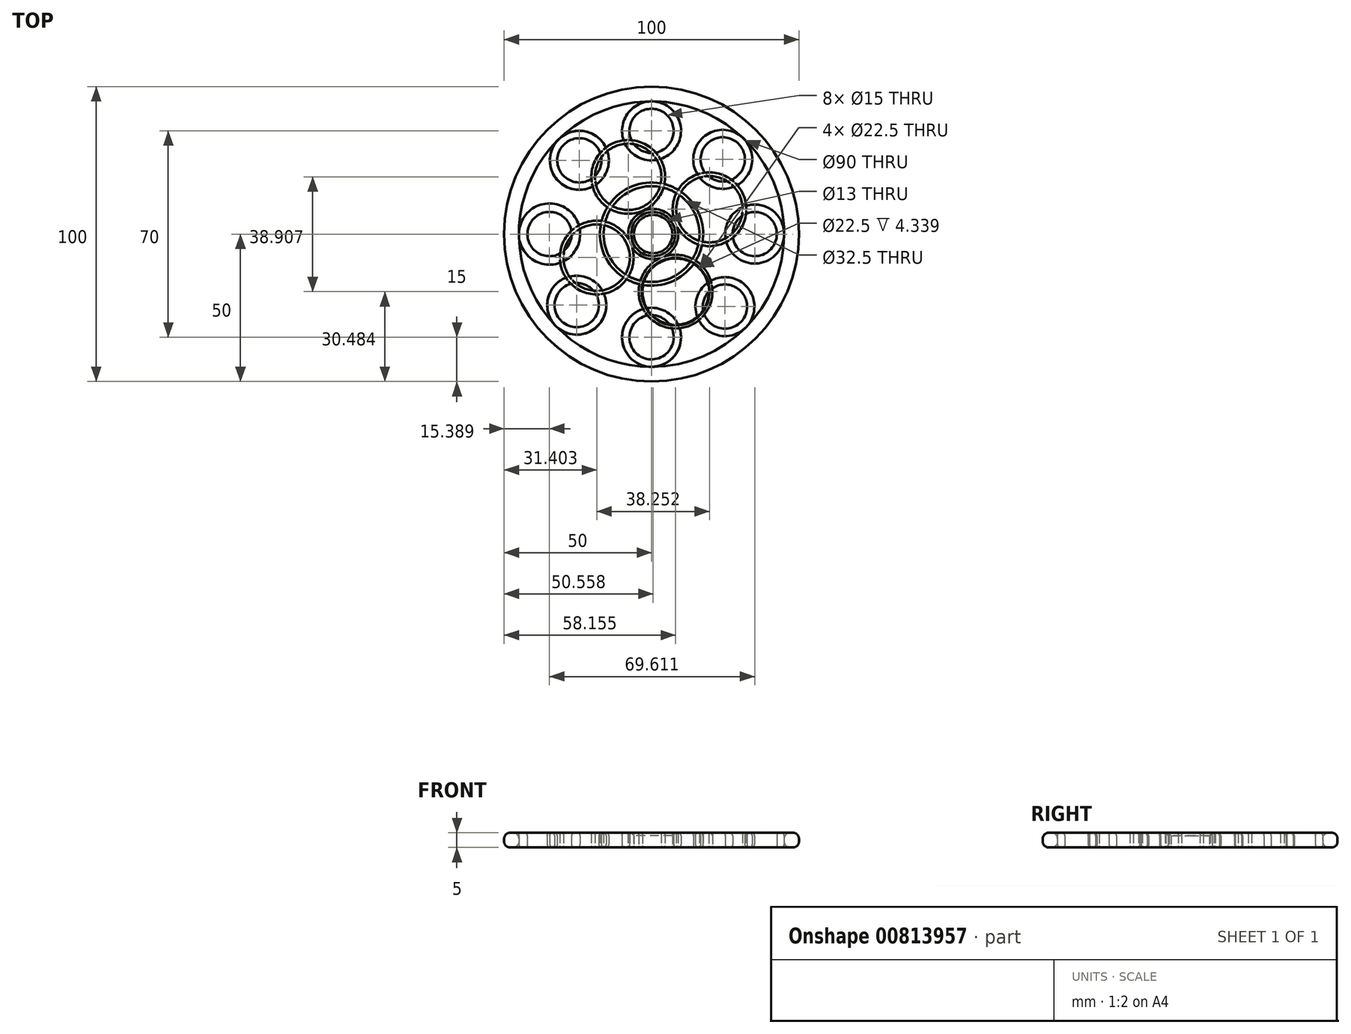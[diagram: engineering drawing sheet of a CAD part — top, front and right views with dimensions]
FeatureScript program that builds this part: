
annotation { "Feature Type Name" : "Feature", "Feature Type Description" : "" }
export const myFeature = defineFeature(function(context is Context, id is Id, definition is map)
    precondition{}
    {
        {
            var Q0;
            Q0=qCreatedBy(makeId("Top.planeOp"),FACE);
            var sketch = newSketch(context, id + "F0", { "sketchPlane" : qUnion([Q0])});
            skCircle(sketch, "E0", {"center": v(0, 0) * mm, "radius": 50 * mm});
            skCircle(sketch, "E1", {"center": v(0, 0) * mm, "radius": 45 * mm});
            skSolve(sketch);
        }
        {
            var Q0;
            Q0=makeQuery(id+"F0.imprint","IMPRINT",FACE,{"disambiguationData":[TD([[makeQuery(id+"F0.imprint","IMPRINT",EDGE,{"derivedFrom":sQuery(id+"F0.wireOp",EDGE,"E0")}),1.0]])]});
            extrude(context, id + "F1", {"entities" : qUnion([Q0]), "depth" : 5 * mm, "offsetDistance" : 25 * mm});
        }
        {
            var Q0;
            Q0=qCreatedBy(makeId("Top.planeOp"),FACE);
            var sketch = newSketch(context, id + "F2", { "sketchPlane" : qUnion([Q0])});
            skCircle(sketch, "E2", {"center": v(35, 0) * mm, "radius": 10 * mm});
            skCircle(sketch, "E3", {"center": v(35, 0) * mm, "radius": 7.5 * mm});
            skSolve(sketch);
        }
        {
            var Q0;
            Q0=makeQuery(id+"F2.imprint","IMPRINT",FACE,{"disambiguationData":[TD([[makeQuery(id+"F2.imprint","IMPRINT",EDGE,{"derivedFrom":sQuery(id+"F2.wireOp",EDGE,"E2")}),1.0]])]});
            extrude(context, id + "F3", {"entities" : qUnion([Q0]), "operationType" : NewBodyOperationType.ADD, "depth" : 5 * mm, "offsetDistance" : 25 * mm});
        }
        {
            var Q0;
            Q0=qCreatedBy(makeId("Top.planeOp"),FACE);
            var sketch = newSketch(context, id + "F4", { "sketchPlane" : qUnion([Q0])});
            skCircle(sketch, "E4", {"center": v(0, 35) * mm, "radius": 10 * mm});
            skCircle(sketch, "E5", {"center": v(0, 35) * mm, "radius": 7.5 * mm});
            skSolve(sketch);
        }
        {
            var Q0;
            Q0=makeQuery(id+"F4.imprint","IMPRINT",FACE,{"disambiguationData":[TD([[makeQuery(id+"F4.imprint","IMPRINT",EDGE,{"derivedFrom":sQuery(id+"F4.wireOp",EDGE,"E4")}),1.0]])]});
            extrude(context, id + "F5", {"entities" : qUnion([Q0]), "operationType" : NewBodyOperationType.ADD, "depth" : 5 * mm, "offsetDistance" : 25 * mm});
        }
        {
            var Q0;
            Q0=qCreatedBy(makeId("Top.planeOp"),FACE);
            var sketch = newSketch(context, id + "F6", { "sketchPlane" : qUnion([Q0])});
            skCircle(sketch, "E6", {"center": v(-34.61, 0) * mm, "radius": 10.39 * mm});
            skCircle(sketch, "E7", {"center": v(-34.61, 0) * mm, "radius": 7.5 * mm});
            skSolve(sketch);
        }
        {
            var Q0;
            Q0=sQuery(id+"F6.wireOp",EDGE,"E6");
            var Q1;
            Q1=sQuery(id+"F6.wireOp",EDGE,"E7");
            extrude(context, id + "F7", {"bodyType" : ToolBodyType.SURFACE, "surfaceEntities" : qUnion([Q0, Q1]), "depth" : 5 * mm, "offsetDistance" : 25 * mm});
        }
        {
            var Q0;
            Q0=makeQuery(id+"F6.imprint","IMPRINT",FACE,{"disambiguationData":[TD([[makeQuery(id+"F6.imprint","IMPRINT",EDGE,{"derivedFrom":sQuery(id+"F6.wireOp",EDGE,"E6")}),1.0]])]});
            extrude(context, id + "F8", {"entities" : qUnion([Q0]), "operationType" : NewBodyOperationType.ADD, "depth" : 5 * mm, "offsetDistance" : 25 * mm});
        }
        {
            var Q0;
            Q0=qCreatedBy(makeId("Top.planeOp"),FACE);
            var sketch = newSketch(context, id + "F9", { "sketchPlane" : qUnion([Q0])});
            skCircle(sketch, "E8", {"center": v(0, -35) * mm, "radius": 10 * mm});
            skCircle(sketch, "E9", {"center": v(0, -35) * mm, "radius": 7.5 * mm});
            skSolve(sketch);
        }
        {
            var Q0;
            Q0=makeQuery(id+"F9.imprint","IMPRINT",FACE,{"disambiguationData":[TD([[makeQuery(id+"F9.imprint","IMPRINT",EDGE,{"derivedFrom":sQuery(id+"F9.wireOp",EDGE,"E8")}),1.0]])]});
            extrude(context, id + "F10", {"entities" : qUnion([Q0]), "operationType" : NewBodyOperationType.ADD, "depth" : 5 * mm, "offsetDistance" : 25 * mm});
        }
        {
            var Q0;
            Q0=qCreatedBy(makeId("Top.planeOp"),FACE);
            var sketch = newSketch(context, id + "F11", { "sketchPlane" : qUnion([Q0])});
            skCircle(sketch, "E10", {"center": v(-25.37, -24.1) * mm, "radius": 10 * mm});
            skCircle(sketch, "E11", {"center": v(-25.37, -24.1) * mm, "radius": 7.5 * mm});
            skSolve(sketch);
        }
        {
            var Q0;
            Q0=makeQuery(id+"F11.imprint","IMPRINT",FACE,{"disambiguationData":[TD([[makeQuery(id+"F11.imprint","IMPRINT",EDGE,{"derivedFrom":sQuery(id+"F11.wireOp",EDGE,"E10")}),1.0]])]});
            extrude(context, id + "F12", {"entities" : qUnion([Q0]), "operationType" : NewBodyOperationType.ADD, "depth" : 5 * mm, "offsetDistance" : 25 * mm});
        }
        {
            var Q0;
            Q0=qCreatedBy(makeId("Top.planeOp"),FACE);
            var sketch = newSketch(context, id + "F13", { "sketchPlane" : qUnion([Q0])});
            skCircle(sketch, "E12", {"center": v(-24.49, 25) * mm, "radius": 10 * mm});
            skCircle(sketch, "E13", {"center": v(-24.49, 25) * mm, "radius": 7.5 * mm});
            skSolve(sketch);
        }
        {
            var Q0;
            Q0=makeQuery(id+"F13.imprint","IMPRINT",FACE,{"disambiguationData":[TD([[makeQuery(id+"F13.imprint","IMPRINT",EDGE,{"derivedFrom":sQuery(id+"F13.wireOp",EDGE,"E12")}),1.0]])]});
            extrude(context, id + "F14", {"entities" : qUnion([Q0]), "operationType" : NewBodyOperationType.ADD, "depth" : 5 * mm, "offsetDistance" : 25 * mm});
        }
        {
            var Q0;
            Q0=qCreatedBy(makeId("Top.planeOp"),FACE);
            var sketch = newSketch(context, id + "F15", { "sketchPlane" : qUnion([Q0])});
            skCircle(sketch, "E14", {"center": v(24.9, -24.6) * mm, "radius": 10 * mm});
            skCircle(sketch, "E15", {"center": v(24.9, -24.6) * mm, "radius": 7.5 * mm});
            skSolve(sketch);
        }
        {
            var Q0;
            Q0=makeQuery(id+"F15.imprint","IMPRINT",FACE,{"disambiguationData":[TD([[makeQuery(id+"F15.imprint","IMPRINT",EDGE,{"derivedFrom":sQuery(id+"F15.wireOp",EDGE,"E14")}),1.0]])]});
            extrude(context, id + "F16", {"entities" : qUnion([Q0]), "operationType" : NewBodyOperationType.ADD, "depth" : 5 * mm, "offsetDistance" : 25 * mm});
        }
        {
            var Q0;
            Q0=qCreatedBy(makeId("Top.planeOp"),FACE);
            var sketch = newSketch(context, id + "F17", { "sketchPlane" : qUnion([Q0])});
            skCircle(sketch, "E16", {"center": v(24.16, 25.32) * mm, "radius": 10 * mm});
            skCircle(sketch, "E17", {"center": v(24.16, 25.32) * mm, "radius": 7.5 * mm});
            skSolve(sketch);
        }
        {
            var Q0;
            Q0=makeQuery(id+"F17.imprint","IMPRINT",FACE,{"disambiguationData":[TD([[makeQuery(id+"F17.imprint","IMPRINT",EDGE,{"derivedFrom":sQuery(id+"F17.wireOp",EDGE,"E16")}),1.0]])]});
            extrude(context, id + "F18", {"entities" : qUnion([Q0]), "operationType" : NewBodyOperationType.ADD, "depth" : 5 * mm, "offsetDistance" : 25 * mm});
        }
        {
            var Q0;
            Q0=qCreatedBy(makeId("Top.planeOp"),FACE);
            var sketch = newSketch(context, id + "F19", { "sketchPlane" : qUnion([Q0])});
            skCircle(sketch, "E18", {"center": v(-18.6, -7.97) * mm, "radius": 12.5 * mm});
            skCircle(sketch, "E19", {"center": v(-18.6, -7.97) * mm, "radius": 11.25 * mm});
            skCircle(sketch, "E20", {"center": v(-18.6, -7.97) * mm, "radius": 7.5 * mm});
            skSolve(sketch);
        }
        {
            var Q0;
            Q0=makeQuery(id+"F19.imprint","IMPRINT",FACE,{"disambiguationData":[TD([[makeQuery(id+"F19.imprint","IMPRINT",EDGE,{"derivedFrom":sQuery(id+"F19.wireOp",EDGE,"E18")}),1.0]])]});
            extrude(context, id + "F20", {"entities" : qUnion([Q0]), "depth" : 5 * mm, "offsetDistance" : 25 * mm});
        }
        {
            var Q0;
            Q0=qCreatedBy(makeId("Top.planeOp"),FACE);
            var sketch = newSketch(context, id + "F21", { "sketchPlane" : qUnion([Q0])});
            skCircle(sketch, "E21", {"center": v(8.16, -19.52) * mm, "radius": 12.5 * mm});
            skCircle(sketch, "E22", {"center": v(8.16, -19.52) * mm, "radius": 11.25 * mm});
            skCircle(sketch, "E23", {"center": v(8.16, -19.52) * mm, "radius": 7.5 * mm});
            skSolve(sketch);
        }
        {
            var Q0;
            Q0=makeQuery(id+"F21.imprint","IMPRINT",FACE,{"disambiguationData":[TD([[makeQuery(id+"F21.imprint","IMPRINT",EDGE,{"derivedFrom":sQuery(id+"F21.wireOp",EDGE,"E21")}),1.0]])]});
            extrude(context, id + "F22", {"entities" : qUnion([Q0]), "depth" : 5 * mm, "offsetDistance" : 25 * mm});
        }
        {
            var Q0;
            Q0=qCreatedBy(makeId("Top.planeOp"),FACE);
            var sketch = newSketch(context, id + "F23", { "sketchPlane" : qUnion([Q0])});
            skCircle(sketch, "E24", {"center": v(19.65, 8.41) * mm, "radius": 12.5 * mm});
            skCircle(sketch, "E25", {"center": v(19.65, 8.41) * mm, "radius": 11.25 * mm});
            skCircle(sketch, "E26", {"center": v(19.65, 8.41) * mm, "radius": 7.5 * mm});
            skSolve(sketch);
        }
        {
            var Q0;
            Q0=makeQuery(id+"F23.imprint","IMPRINT",FACE,{"disambiguationData":[TD([[makeQuery(id+"F23.imprint","IMPRINT",EDGE,{"derivedFrom":sQuery(id+"F23.wireOp",EDGE,"E24")}),1.0]])]});
            var Q1;
            Q1 = qSketchRegion(id + "F21", true);
            extrude(context, id + "F24", {"entities" : qUnion([Q0, Q1]), "depth" : 5 * mm, "offsetDistance" : 25 * mm});
        }
        {
            var Q0;
            Q0=qCreatedBy(makeId("Top.planeOp"),FACE);
            var sketch = newSketch(context, id + "F25", { "sketchPlane" : qUnion([Q0])});
            skCircle(sketch, "E27", {"center": v(-7.91, 19.4) * mm, "radius": 12.5 * mm});
            skCircle(sketch, "E28", {"center": v(-7.91, 19.4) * mm, "radius": 11.25 * mm});
            skCircle(sketch, "E29", {"center": v(-7.91, 19.4) * mm, "radius": 7.5 * mm});
            skSolve(sketch);
        }
        {
            var Q0;
            Q0=makeQuery(id+"F25.imprint","IMPRINT",FACE,{"disambiguationData":[TD([[makeQuery(id+"F25.imprint","IMPRINT",EDGE,{"derivedFrom":sQuery(id+"F25.wireOp",EDGE,"E27")}),1.0]])]});
            extrude(context, id + "F26", {"entities" : qUnion([Q0]), "depth" : 5 * mm, "offsetDistance" : 25 * mm});
        }
        {
            var Q0;
            Q0=qCreatedBy(makeId("Top.planeOp"),FACE);
            var sketch = newSketch(context, id + "F27", { "sketchPlane" : qUnion([Q0])});
            skCircle(sketch, "E30", {"center": v(0, 0) * mm, "radius": 17.5 * mm});
            skCircle(sketch, "E31", {"center": v(0, 0) * mm, "radius": 16.25 * mm});
            skCircle(sketch, "E32", {"center": v(0, 0) * mm, "radius": 8.5 * mm});
            skCircle(sketch, "E33", {"center": v(0, 0) * mm, "radius": 4.68 * mm});
            skSolve(sketch);
        }
        {
            var Q0;
            Q0=makeQuery(id+"F27.imprint","IMPRINT",FACE,{"disambiguationData":[TD([[makeQuery(id+"F27.imprint","IMPRINT",EDGE,{"derivedFrom":sQuery(id+"F27.wireOp",EDGE,"E30")}),1.0]])]});
            extrude(context, id + "F28", {"entities" : qUnion([Q0]), "depth" : 5 * mm, "offsetDistance" : 25 * mm});
        }
        {
            var Q0;
            Q0=qCreatedBy(makeId("Top.planeOp"),FACE);
            var sketch = newSketch(context, id + "F29", { "sketchPlane" : qUnion([Q0])});
            skCircle(sketch, "E34", {"center": v(0.56, 0) * mm, "radius": 8.5 * mm});
            skCircle(sketch, "E35", {"center": v(0.56, 0) * mm, "radius": 6.5 * mm});
            skSolve(sketch);
        }
        {
            var Q0;
            Q0=makeQuery(id+"F29.imprint","IMPRINT",FACE,{"disambiguationData":[TD([[makeQuery(id+"F29.imprint","IMPRINT",EDGE,{"derivedFrom":sQuery(id+"F29.wireOp",EDGE,"E34")}),1.0]])]});
            extrude(context, id + "F30", {"entities" : qUnion([Q0]), "depth" : 5 * mm, "offsetDistance" : 25 * mm});
        }
        {
            var Q0;
            Q0=makeQuery(id+"F30.opExtrude","CAP_EDGE",EDGE,{"disambiguationData":[OSD([sQuery(id+"F29.wireOp",EDGE,"E35")])],"isStart":false});
            chamfer(context, id + "F31", {"entities" : qUnion([Q0]), "width" : 1 * mm, "tangentPropagation" : true});
        }
        {
            var Q0;
            Q0=makeQuery(id+"F12.opExtrude","CAP_EDGE",EDGE,{"disambiguationData":[OSD([sQuery(id+"F11.wireOp",EDGE,"E10")])],"isStart":false});
            var Q1;
            Q1=makeQuery(id+"F12.opExtrude","CAP_EDGE",EDGE,{"disambiguationData":[OSD([sQuery(id+"F11.wireOp",EDGE,"E11")])],"isStart":false});
            var Q2;
            Q2=makeQuery(id+"F10.opExtrude","CAP_EDGE",EDGE,{"disambiguationData":[OSD([sQuery(id+"F9.wireOp",EDGE,"E9")])],"isStart":false});
            var Q3;
            Q3=makeQuery(id+"F10.opExtrude","CAP_EDGE",EDGE,{"disambiguationData":[OSD([sQuery(id+"F9.wireOp",EDGE,"E8")])],"isStart":false});
            var Q4;
            Q4=makeQuery(id+"F16.opExtrude","CAP_EDGE",EDGE,{"disambiguationData":[OSD([sQuery(id+"F15.wireOp",EDGE,"E14")])],"isStart":false});
            var Q5;
            Q5=makeQuery(id+"F16.opExtrude","CAP_EDGE",EDGE,{"disambiguationData":[OSD([sQuery(id+"F15.wireOp",EDGE,"E15")])],"isStart":false});
            var Q6;
            Q6=makeQuery(id+"F3.opExtrude","CAP_EDGE",EDGE,{"disambiguationData":[OSD([sQuery(id+"F2.wireOp",EDGE,"E2")])],"isStart":false});
            var Q7;
            Q7=makeQuery(id+"F3.opExtrude","CAP_EDGE",EDGE,{"disambiguationData":[OSD([sQuery(id+"F2.wireOp",EDGE,"E3")])],"isStart":false});
            var Q8;
            Q8=makeQuery(id+"F18.opExtrude","CAP_EDGE",EDGE,{"disambiguationData":[OSD([sQuery(id+"F17.wireOp",EDGE,"E16")])],"isStart":false});
            var Q9;
            Q9=makeQuery(id+"F18.opExtrude","CAP_EDGE",EDGE,{"disambiguationData":[OSD([sQuery(id+"F17.wireOp",EDGE,"E17")])],"isStart":false});
            var Q10;
            Q10=makeQuery(id+"F5.opExtrude","CAP_EDGE",EDGE,{"disambiguationData":[OSD([sQuery(id+"F4.wireOp",EDGE,"E4")])],"isStart":false});
            var Q11;
            Q11=makeQuery(id+"F5.opExtrude","CAP_EDGE",EDGE,{"disambiguationData":[OSD([sQuery(id+"F4.wireOp",EDGE,"E5")])],"isStart":false});
            var Q12;
            Q12=makeQuery(id+"F14.opExtrude","CAP_EDGE",EDGE,{"disambiguationData":[OSD([sQuery(id+"F13.wireOp",EDGE,"E12")])],"isStart":false});
            var Q13;
            Q13=makeQuery(id+"F14.opExtrude","CAP_EDGE",EDGE,{"disambiguationData":[OSD([sQuery(id+"F13.wireOp",EDGE,"E13")])],"isStart":false});
            fillet(context, id + "F32", {"entities" : qUnion([Q0, Q1, Q2, Q3, Q4, Q5, Q6, Q7, Q8, Q9, Q10, Q11, Q12, Q13]), "radius" : 1 * mm, "tangentPropagation" : true, "allowEdgeOverflow" : false});
        }
        {
            var Q0;
            Q0=makeQuery(id+"F8.opExtrude","CAP_FACE",FACE,{"disambiguationData":[OSD([sQuery(id+"F6.wireOp",EDGE,"E6"),sQuery(id+"F6.wireOp",EDGE,"E7")])],"isStart":false});
            fillet(context, id + "F33", {"entities" : qUnion([Q0]), "radius" : 1 * mm, "tangentPropagation" : true, "allowEdgeOverflow" : false});
        }
        {
            var Q0;
            Q0=makeQuery(id+"F1.opExtrude","CAP_EDGE",EDGE,{"disambiguationData":[OSD([sQuery(id+"F0.wireOp",EDGE,"E1")])],"isStart":false});
            var Q1;
            Q1=makeQuery(id+"F1.opExtrude","CAP_EDGE",EDGE,{"disambiguationData":[OSD([sQuery(id+"F0.wireOp",EDGE,"E0")])],"isStart":false});
            fillet(context, id + "F34", {"entities" : qUnion([Q0, Q1]), "radius" : 2 * mm, "tangentPropagation" : true, "allowEdgeOverflow" : false});
        }
        {
            var Q0;
            Q0=makeQuery(id+"F22.opExtrude","CAP_EDGE",EDGE,{"disambiguationData":[OSD([sQuery(id+"F21.wireOp",EDGE,"E21")])],"isStart":false});
            var Q1;
            Q1=makeQuery(id+"F22.opExtrude","CAP_EDGE",EDGE,{"disambiguationData":[OSD([sQuery(id+"F21.wireOp",EDGE,"E22")])],"isStart":false});
            var Q2;
            Q2=makeQuery(id+"F28.opExtrude","CAP_EDGE",EDGE,{"disambiguationData":[OSD([sQuery(id+"F27.wireOp",EDGE,"E30")])],"isStart":false});
            var Q3;
            Q3=makeQuery(id+"F28.opExtrude","CAP_EDGE",EDGE,{"disambiguationData":[OSD([sQuery(id+"F27.wireOp",EDGE,"E31")])],"isStart":false});
            var Q4;
            Q4=makeQuery(id+"F20.opExtrude","CAP_EDGE",EDGE,{"disambiguationData":[OSD([sQuery(id+"F19.wireOp",EDGE,"E18")])],"isStart":false});
            var Q5;
            Q5=makeQuery(id+"F20.opExtrude","CAP_EDGE",EDGE,{"disambiguationData":[OSD([sQuery(id+"F19.wireOp",EDGE,"E19")])],"isStart":false});
            var Q6;
            Q6=makeQuery(id+"F24.opExtrude","CAP_EDGE",EDGE,{"disambiguationData":[OSD([sQuery(id+"F23.wireOp",EDGE,"E24")])],"isStart":false});
            var Q7;
            Q7=makeQuery(id+"F24.opExtrude","CAP_EDGE",EDGE,{"disambiguationData":[OSD([sQuery(id+"F23.wireOp",EDGE,"E25")])],"isStart":false});
            var Q8;
            Q8=makeQuery(id+"F26.opExtrude","CAP_EDGE",EDGE,{"disambiguationData":[OSD([sQuery(id+"F25.wireOp",EDGE,"E28")])],"isStart":false});
            var Q9;
            Q9=makeQuery(id+"F26.opExtrude","CAP_EDGE",EDGE,{"disambiguationData":[OSD([sQuery(id+"F25.wireOp",EDGE,"E27")])],"isStart":false});
            var Q10;
            Q10=makeQuery(id+"F30.opExtrude","CAP_EDGE",EDGE,{"disambiguationData":[OSD([sQuery(id+"F29.wireOp",EDGE,"E34")])],"isStart":false});
            fillet(context, id + "F35", {"entities" : qUnion([Q0, Q1, Q2, Q3, Q4, Q5, Q6, Q7, Q8, Q9, Q10]), "radius" : .5 * mm, "tangentPropagation" : true, "allowEdgeOverflow" : false});
        }
        {
            var Q0;
            Q0=makeQuery(id+"F1.opExtrude","CAP_EDGE",EDGE,{"disambiguationData":[OSD([sQuery(id+"F0.wireOp",EDGE,"E0")])],"isStart":true});
            var Q1;
            Q1=makeQuery(id+"F1.opExtrude","CAP_EDGE",EDGE,{"disambiguationData":[OSD([sQuery(id+"F0.wireOp",EDGE,"E1")])],"isStart":true});
            fillet(context, id + "F36", {"entities" : qUnion([Q0, Q1]), "radius" : 2 * mm, "tangentPropagation" : true, "allowEdgeOverflow" : false});
        }
        {
            var Q0;
            Q0=makeQuery(id+"F14.opExtrude","CAP_EDGE",EDGE,{"disambiguationData":[OSD([sQuery(id+"F13.wireOp",EDGE,"E12")])],"isStart":true});
            var Q1;
            Q1=makeQuery(id+"F14.opExtrude","CAP_EDGE",EDGE,{"disambiguationData":[OSD([sQuery(id+"F13.wireOp",EDGE,"E13")])],"isStart":true});
            var Q2;
            Q2=makeQuery(id+"F5.opExtrude","CAP_EDGE",EDGE,{"disambiguationData":[OSD([sQuery(id+"F4.wireOp",EDGE,"E5")])],"isStart":true});
            var Q3;
            Q3=makeQuery(id+"F5.opExtrude","CAP_EDGE",EDGE,{"disambiguationData":[OSD([sQuery(id+"F4.wireOp",EDGE,"E4")])],"isStart":true});
            var Q4;
            Q4=makeQuery(id+"F18.opExtrude","CAP_EDGE",EDGE,{"disambiguationData":[OSD([sQuery(id+"F17.wireOp",EDGE,"E17")])],"isStart":true});
            var Q5;
            Q5=makeQuery(id+"F18.opExtrude","CAP_EDGE",EDGE,{"disambiguationData":[OSD([sQuery(id+"F17.wireOp",EDGE,"E16")])],"isStart":true});
            var Q6;
            Q6=makeQuery(id+"F3.opExtrude","CAP_EDGE",EDGE,{"disambiguationData":[OSD([sQuery(id+"F2.wireOp",EDGE,"E2")])],"isStart":true});
            var Q7;
            Q7=makeQuery(id+"F3.opExtrude","CAP_EDGE",EDGE,{"disambiguationData":[OSD([sQuery(id+"F2.wireOp",EDGE,"E3")])],"isStart":true});
            var Q8;
            Q8=makeQuery(id+"F16.opExtrude","CAP_EDGE",EDGE,{"disambiguationData":[OSD([sQuery(id+"F15.wireOp",EDGE,"E14")])],"isStart":true});
            var Q9;
            Q9=makeQuery(id+"F16.opExtrude","CAP_EDGE",EDGE,{"disambiguationData":[OSD([sQuery(id+"F15.wireOp",EDGE,"E15")])],"isStart":true});
            var Q10;
            Q10=makeQuery(id+"F10.opExtrude","CAP_EDGE",EDGE,{"disambiguationData":[OSD([sQuery(id+"F9.wireOp",EDGE,"E8")])],"isStart":true});
            var Q11;
            Q11=makeQuery(id+"F10.opExtrude","CAP_EDGE",EDGE,{"disambiguationData":[OSD([sQuery(id+"F9.wireOp",EDGE,"E9")])],"isStart":true});
            var Q12;
            Q12=makeQuery(id+"F12.opExtrude","CAP_EDGE",EDGE,{"disambiguationData":[OSD([sQuery(id+"F11.wireOp",EDGE,"E10")])],"isStart":true});
            var Q13;
            Q13=makeQuery(id+"F12.opExtrude","CAP_EDGE",EDGE,{"disambiguationData":[OSD([sQuery(id+"F11.wireOp",EDGE,"E11")])],"isStart":true});
            var Q14;
            Q14=makeQuery(id+"F8.opExtrude","CAP_FACE",FACE,{"disambiguationData":[OSD([sQuery(id+"F6.wireOp",EDGE,"E6"),sQuery(id+"F6.wireOp",EDGE,"E7")])],"isStart":true});
            fillet(context, id + "F37", {"entities" : qUnion([Q0, Q1, Q2, Q3, Q4, Q5, Q6, Q7, Q8, Q9, Q10, Q11, Q12, Q13, Q14]), "radius" : 1 * mm, "tangentPropagation" : true, "allowEdgeOverflow" : false});
        }
        {
            var Q0;
            Q0=makeQuery(id+"F26.opExtrude","CAP_EDGE",EDGE,{"disambiguationData":[OSD([sQuery(id+"F25.wireOp",EDGE,"E27")])],"isStart":true});
            var Q1;
            Q1=makeQuery(id+"F26.opExtrude","CAP_EDGE",EDGE,{"disambiguationData":[OSD([sQuery(id+"F25.wireOp",EDGE,"E28")])],"isStart":true});
            var Q2;
            Q2=makeQuery(id+"F24.opExtrude","CAP_EDGE",EDGE,{"disambiguationData":[OSD([sQuery(id+"F23.wireOp",EDGE,"E25")])],"isStart":true});
            var Q3;
            Q3=makeQuery(id+"F24.opExtrude","CAP_EDGE",EDGE,{"disambiguationData":[OSD([sQuery(id+"F23.wireOp",EDGE,"E24")])],"isStart":true});
            var Q4;
            Q4=makeQuery(id+"F22.opExtrude","CAP_EDGE",EDGE,{"disambiguationData":[OSD([sQuery(id+"F21.wireOp",EDGE,"E22")])],"isStart":true});
            var Q5;
            Q5=makeQuery(id+"F22.opExtrude","CAP_EDGE",EDGE,{"disambiguationData":[OSD([sQuery(id+"F21.wireOp",EDGE,"E21")])],"isStart":true});
            var Q6;
            Q6=makeQuery(id+"F20.opExtrude","CAP_EDGE",EDGE,{"disambiguationData":[OSD([sQuery(id+"F19.wireOp",EDGE,"E18")])],"isStart":true});
            var Q7;
            Q7=makeQuery(id+"F28.opExtrude","CAP_EDGE",EDGE,{"disambiguationData":[OSD([sQuery(id+"F27.wireOp",EDGE,"E30")])],"isStart":true});
            var Q8;
            Q8=makeQuery(id+"F28.opExtrude","CAP_EDGE",EDGE,{"disambiguationData":[OSD([sQuery(id+"F27.wireOp",EDGE,"E31")])],"isStart":true});
            var Q9;
            Q9=makeQuery(id+"F20.opExtrude","CAP_EDGE",EDGE,{"disambiguationData":[OSD([sQuery(id+"F19.wireOp",EDGE,"E19")])],"isStart":true});
            fillet(context, id + "F38", {"entities" : qUnion([Q0, Q1, Q2, Q3, Q4, Q5, Q6, Q7, Q8, Q9]), "radius" : .5 * mm, "tangentPropagation" : true, "allowEdgeOverflow" : false});
        }
        {
            var Q0;
            Q0=makeQuery(id+"F30.opExtrude","CAP_EDGE",EDGE,{"disambiguationData":[OSD([sQuery(id+"F29.wireOp",EDGE,"E34")])],"isStart":true});
            var Q1;
            Q1=makeQuery(id+"F30.opExtrude","CAP_EDGE",EDGE,{"disambiguationData":[OSD([sQuery(id+"F29.wireOp",EDGE,"E35")])],"isStart":true});
            fillet(context, id + "F39", {"entities" : qUnion([Q0, Q1]), "radius" : .5 * mm, "tangentPropagation" : true, "allowEdgeOverflow" : false});
        }
        {
            var Q0;
            Q0=makeQuery(id+"F24.opExtrude","CAP_EDGE",EDGE,{"disambiguationData":[OSD([sQuery(id+"F21.wireOp",EDGE,"E21")])],"isStart":false});
            fillet(context, id + "F40", {"entities" : qUnion([Q0]), "radius" : 1 * mm, "tangentPropagation" : true, "allowEdgeOverflow" : false});
        }
        {
            var Q0;
            Q0=makeQuery(id+"F24.opExtrude","CAP_EDGE",EDGE,{"disambiguationData":[OSD([sQuery(id+"F21.wireOp",EDGE,"E22")])],"isStart":false});
            fillet(context, id + "F41", {"entities" : qUnion([Q0]), "radius" : 1 * mm, "tangentPropagation" : true, "allowEdgeOverflow" : false});
        }
    });
